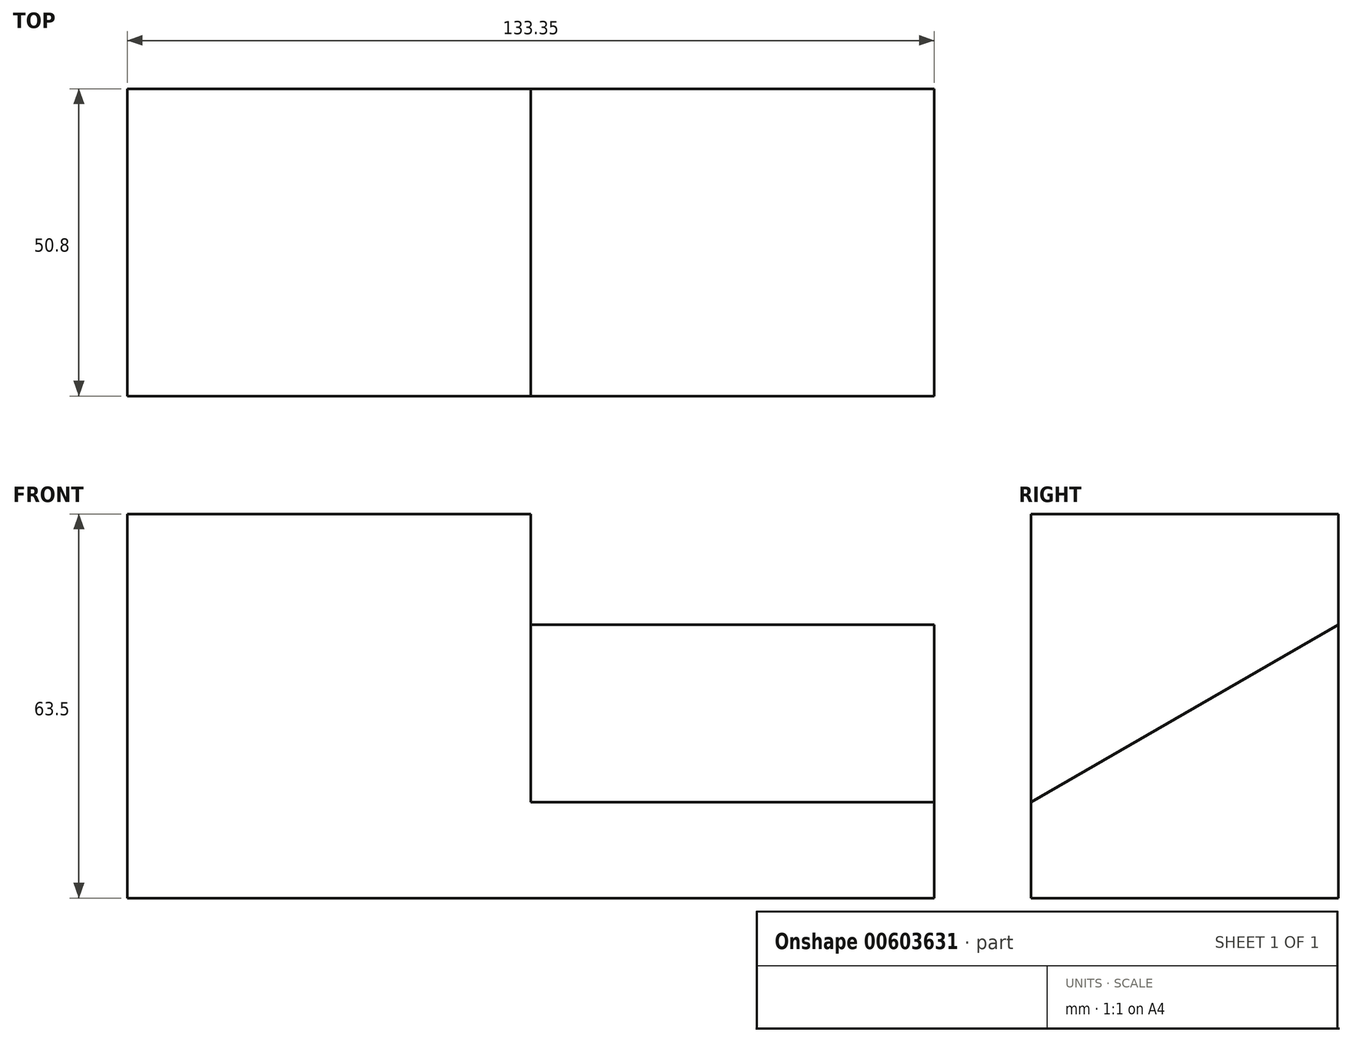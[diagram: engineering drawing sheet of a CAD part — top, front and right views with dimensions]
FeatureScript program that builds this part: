
annotation { "Feature Type Name" : "Feature", "Feature Type Description" : "" }
export const myFeature = defineFeature(function(context is Context, id is Id, definition is map)
    precondition{}
    {
        {
            var Q0;
            Q0=qCreatedBy(makeId("Front.planeOp"),FACE);
            var sketch = newSketch(context, id + "F0", { "sketchPlane" : qUnion([Q0])});
            skLineSegment(sketch, "E0.bottom", {"start": v(-25.68, 72.58) * mm, "end": v(107.67, 72.58) * mm});
            skLineSegment(sketch, "E0.top", {"start": v(-25.68, 9.08) * mm, "end": v(107.67, 9.08) * mm});
            skLineSegment(sketch, "E0.left", {"start": v(-25.68, 72.58) * mm, "end": v(-25.68, 9.08) * mm});
            skLineSegment(sketch, "E0.right", {"start": v(107.67, 72.58) * mm, "end": v(107.67, 9.08) * mm});
            skSolve(sketch);
        }
        {
            var Q0;
            Q0 = qSketchRegion(id + "F0", true);
            extrude(context, id + "F1", {"entities" : qUnion([Q0]), "depth" : 50.8 * mm, "offsetDistance" : 25.4 * mm});
        }
        {
            var Q0;
            Q0=makeQuery(id+"F1.opExtrude","SWEPT_FACE",FACE,{"disambiguationData":[OSD([sQuery(id+"F0.wireOp",EDGE,"E0.right")])]});
            var sketch = newSketch(context, id + "F2", { "sketchPlane" : qUnion([Q0])});
            skLineSegment(sketch, "E1", {"start": v(-50.8, 24.95) * mm, "end": v(0, 54.28) * mm});
            skLineSegment(sketch, "E2", {"start": v(0, 72.58) * mm, "end": v(-50.8, 72.58) * mm});
            skLineSegment(sketch, "E3", {"start": v(-50.8, 72.58) * mm, "end": v(-50.8, 24.95) * mm});
            skSolve(sketch);
        }
        {
            var Q0;
            {var subQ0=sQuery(id+"F2.wireOp",EDGE,"E1");Q0=makeQuery(id+"F2.imprint","IMPRINT",FACE,{"disambiguationData":[TD([[makeQuery(id+"F2.imprint","IMPRINT",EDGE,{"derivedFrom":subQ0}),1.0]])]});}
            extrude(context, id + "F3", {"entities" : qUnion([Q0]), "operationType" : NewBodyOperationType.REMOVE, "depth" : -66.67 * mm, "offsetDistance" : 25.4 * mm});
        }
    });
